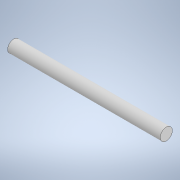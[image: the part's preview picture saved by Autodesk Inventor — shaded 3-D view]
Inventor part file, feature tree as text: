
AUTODESK INVENTOR PART (.ipt)
format: ipt  version: 2020 (Build 240168000, 168)  size: 94,208 bytes
history: native  units: mm
features: sketch x2, extrude x1
ambient origin geometry x8: Origin, YZ Plane, XZ Plane, XY Plane, X Axis, Y Axis, Z Axis, Center Point
bodies: Body1 (feature_tree)
feature tree (3):
  sketch  "Szkic1"
  sketch  "Szkic 3D1"
  extrude  "Wyciągnięcie proste2"  Depth=3.0mm
